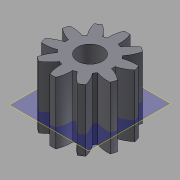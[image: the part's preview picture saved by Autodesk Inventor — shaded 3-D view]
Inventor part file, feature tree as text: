
AUTODESK INVENTOR PART (.ipt)
format: ipt  version: 2015 (Build 190159000, 159)  size: 161,792 bytes
history: native  units: in
note: dims shown in document units (in); Inventor stores cm internally (conversion verified against a paired STEP export)
features: other x13, sketch x3, plane x2
ambient origin geometry x8: Origin, YZ Plane, XZ Plane, XY Plane, X Axis, Y Axis, Z Axis, Center Point
bodies: Solid1 (feature_tree)
feature tree (18):
  other  "Spur Gear1"
  other  "Solid1::Spur Gear1"
  other  "TaggingFeature1"
  sketch  "Sketch1"  dims[d0=0.3937in]
  sketch  "Sketch2"  dims[d16=0.4724in d17=0.0in d41=0.0in d43=0.4724in d46=0.4724in d47=0.0in d48=0.0in]
  sketch  "Sketch3"
  plane  "XZ Plane_1"
  plane  "Work Plane2"
  other  "Z Axis_1"
  other  "Srf1"
  other  "Srf1::Derived"
  other  "Distance iMate"
  other  "Align iMate"
  other  "Mesh iMate"
  other  "Axis iMate"
  other  "Position iMate"
  other  "Mesh iMate2"
  other  "Start plane iMate"
